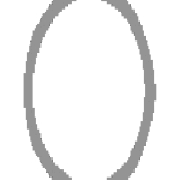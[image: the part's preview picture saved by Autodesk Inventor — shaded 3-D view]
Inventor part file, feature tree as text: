
AUTODESK INVENTOR PART (.ipt)
format: ipt  version: 2021 (Build 250183000, 183)  size: 118,784 bytes
history: native  units: in
note: dims shown in document units (in); Inventor stores cm internally (conversion verified against a paired STEP export)
features: other x4, sketch x3, plane x1
ambient origin geometry x8: Origin, YZ Plane, XZ Plane, XY Plane, X Axis, Y Axis, Z Axis, Center Point
bodies: Solid1 (feature_tree), Body (feature_tree)
feature tree (8):
  other  "Driven Length"
  other  "Frame Generator"
  other  "Start Plane"
  other  "End Plane"
  sketch  "Sketch"  dims[d2=0.5in d4=-0.0in d5=0.5in d6=0.12in d7=0.0in d8=90.0deg d9=0.5in]
  sketch  "Sketch2"  dims[d0=1.0in]
  plane  "Work Plane3"
  sketch  "Sketch3"  dims[d1=0.065in]
